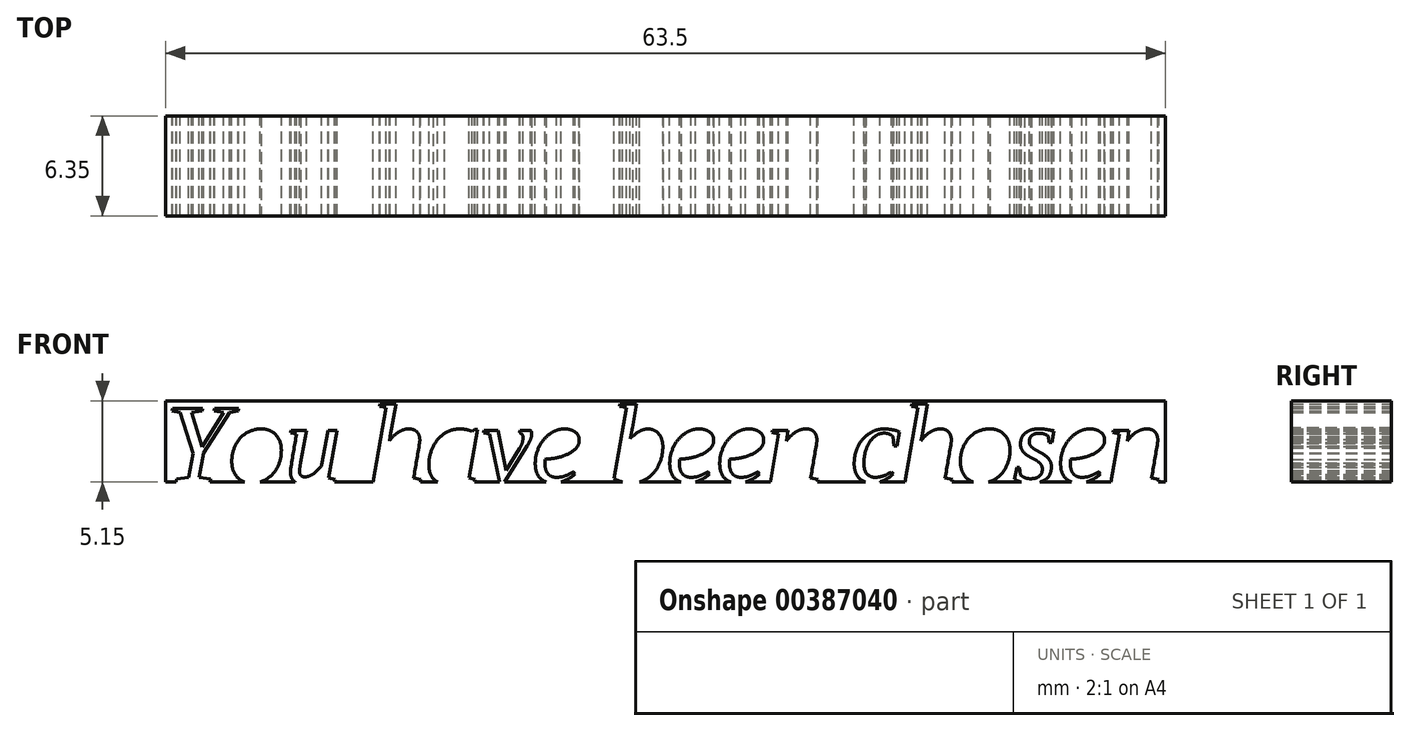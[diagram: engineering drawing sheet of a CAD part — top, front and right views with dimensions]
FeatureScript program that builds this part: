
annotation { "Feature Type Name" : "Feature", "Feature Type Description" : "" }
export const myFeature = defineFeature(function(context is Context, id is Id, definition is map)
    precondition{}
    {
        {
            var Q0;
            Q0=qCreatedBy(makeId("Front.planeOp"),FACE);
            var sketch = newSketch(context, id + "F0", { "sketchPlane" : qUnion([Q0])});
            skText(sketch, "E0", { "text": "You have been chosen", "fontName": "Tinos-Italic.ttf"});
            skLineSegment(sketch, "E1.bottom", {"start": v(-313.5, 5.15) * mm, "end": v(-250, 5.15) * mm});
            skLineSegment(sketch, "E1.top", {"start": v(-313.5, 0) * mm, "end": v(-250, 0) * mm});
            skLineSegment(sketch, "E1.left", {"start": v(-313.5, 5.15) * mm, "end": v(-313.5, 0) * mm});
            skLineSegment(sketch, "E1.right", {"start": v(-250, 5.15) * mm, "end": v(-250, 0) * mm});
            const initialGuessF0  = {"E0": [-0.3135, 0, 1, 0, 0.00515]};
            skSetInitialGuess(sketch, initialGuessF0);
            skSolve(sketch);
        }
        {
            var Q0;
            Q0=makeQuery(id+"F0.imprint","IMPRINT",FACE,{"disambiguationData":[TD([[makeQuery(id+"F0.imprint","IMPRINT",EDGE,{"derivedFrom":sQuery(id+"F0.wireOp",EDGE,"E0.sketch_text.stroke-0")}),1.0]])]});
            extrude(context, id + "F1", {"entities" : qUnion([Q0]), "depth" : 6.35 * mm});
        }
    });
